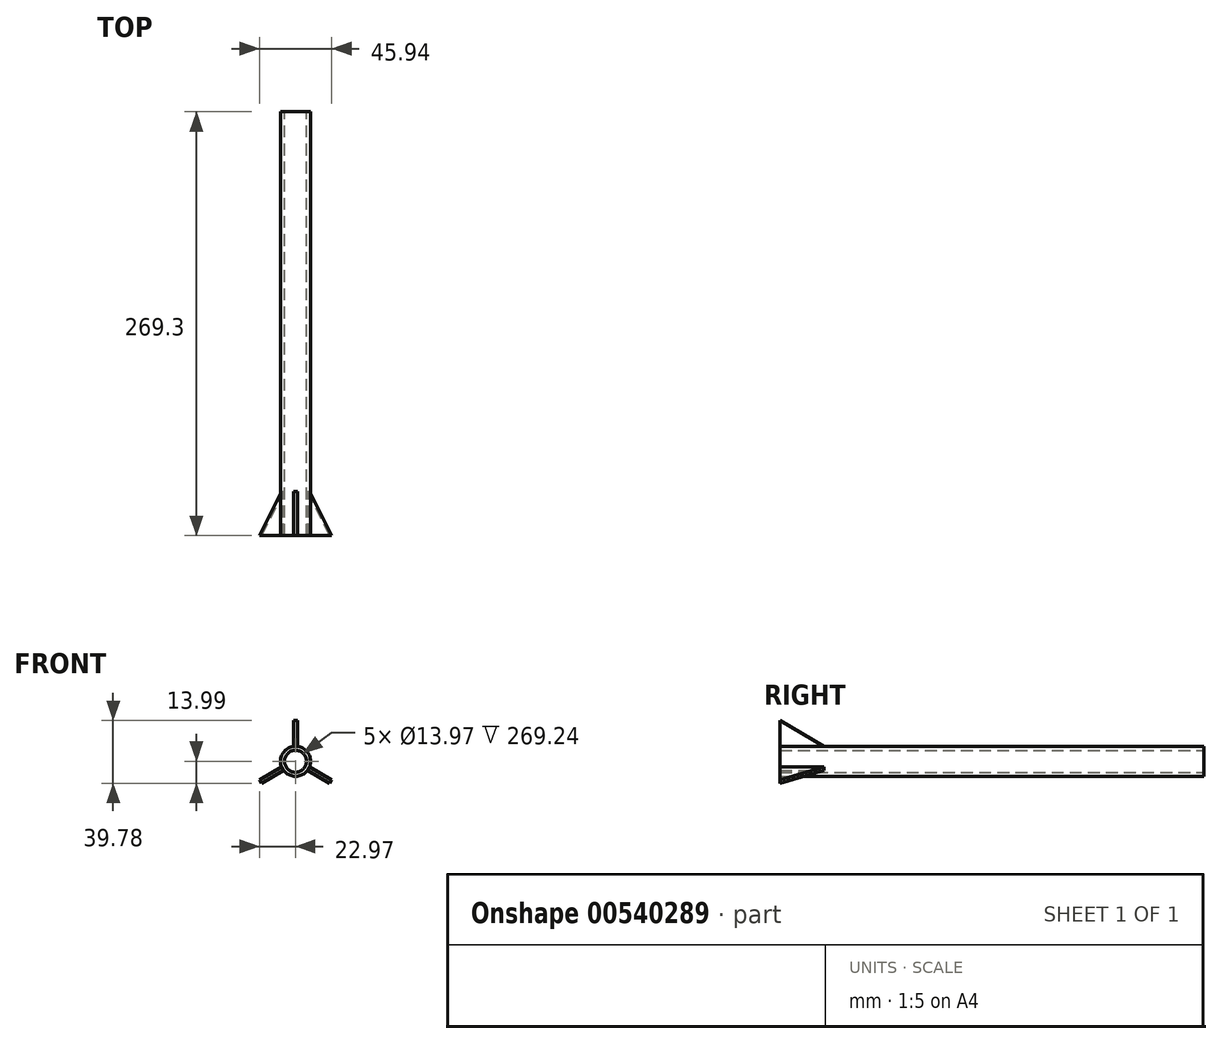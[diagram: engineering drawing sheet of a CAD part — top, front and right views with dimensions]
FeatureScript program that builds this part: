
annotation { "Feature Type Name" : "Feature", "Feature Type Description" : "" }
export const myFeature = defineFeature(function(context is Context, id is Id, definition is map)
    precondition{}
    {
        {
            var Q0;
            Q0=qCreatedBy(makeId("Front.planeOp"),FACE);
            var sketch = newSketch(context, id + "F0", { "sketchPlane" : qUnion([Q0])});
            skCircle(sketch, "E0", {"center": v(0, 0) * mm, "radius": 9.53 * mm});
            skCircle(sketch, "E1", {"center": v(0, 0) * mm, "radius": 6.99 * mm});
            skSolve(sketch);
        }
        {
            var Q0;
            Q0 = qSketchRegion(id + "F0", true);
            extrude(context, id + "F1", {"entities" : qUnion([Q0]), "depth" : 269.24 * mm, "offsetDistance" : 25.4 * mm, "symmetric" : true});
        }
        {
            var Q0;
            Q0=qCreatedBy(makeId("Right.planeOp"),FACE);
            var sketch = newSketch(context, id + "F2", { "sketchPlane" : qUnion([Q0])});
            skLineSegment(sketch, "E2", {"start": v(-134.56, 9.54) * mm, "end": v(-106.76, 9.54) * mm});
            skLineSegment(sketch, "E3", {"start": v(-106.76, 9.54) * mm, "end": v(-134.68, 25.79) * mm});
            skLineSegment(sketch, "E4", {"start": v(-134.68, 25.79) * mm, "end": v(-134.56, 9.54) * mm});
            skSolve(sketch);
        }
        {
            var Q0;
            Q0 = qSketchRegion(id + "F2", true);
            extrude(context, id + "F3", {"entities" : qUnion([Q0]), "depth" : 2.54 * mm, "offsetDistance" : 25.4 * mm, "symmetric" : true});
        }
        {
            var Q0;
            Q0=makeQuery(id+"F3.opExtrude","SWEPT_BODY",BODY,{"disambiguationData":[OSD([sQuery(id+"F2.wireOp",EDGE,"E2"),sQuery(id+"F2.wireOp",EDGE,"E3"),sQuery(id+"F2.wireOp",EDGE,"E4")])]});
            var Q1;
            Q1=makeQuery(id+"F1.opExtrude","CAP_EDGE",EDGE,{"disambiguationData":[OSD([sQuery(id+"F0.wireOp",EDGE,"E0")])],"isStart":false});
            transform(context, id + "F4", {"entities" : qUnion([Q0]), "transformType" : TransformType.ROTATION, "transformAxis" : qUnion([Q1]), "angle" : 120 * degree, "makeCopy" : true});
        }
        {
            var Q0;
            Q0=makeQuery(id+"F3.opExtrude","SWEPT_BODY",BODY,{"disambiguationData":[OSD([sQuery(id+"F2.wireOp",EDGE,"E2"),sQuery(id+"F2.wireOp",EDGE,"E3"),sQuery(id+"F2.wireOp",EDGE,"E4")])]});
            var Q1;
            Q1=makeQuery(id+"F1.opExtrude","CAP_EDGE",EDGE,{"disambiguationData":[OSD([sQuery(id+"F0.wireOp",EDGE,"E0")])],"isStart":false});
            transform(context, id + "F5", {"entities" : qUnion([Q0]), "transformType" : TransformType.ROTATION, "transformAxis" : qUnion([Q1]), "angle" : 120 * degree, "oppositeDirection" : true, "makeCopy" : true});
        }
    });
